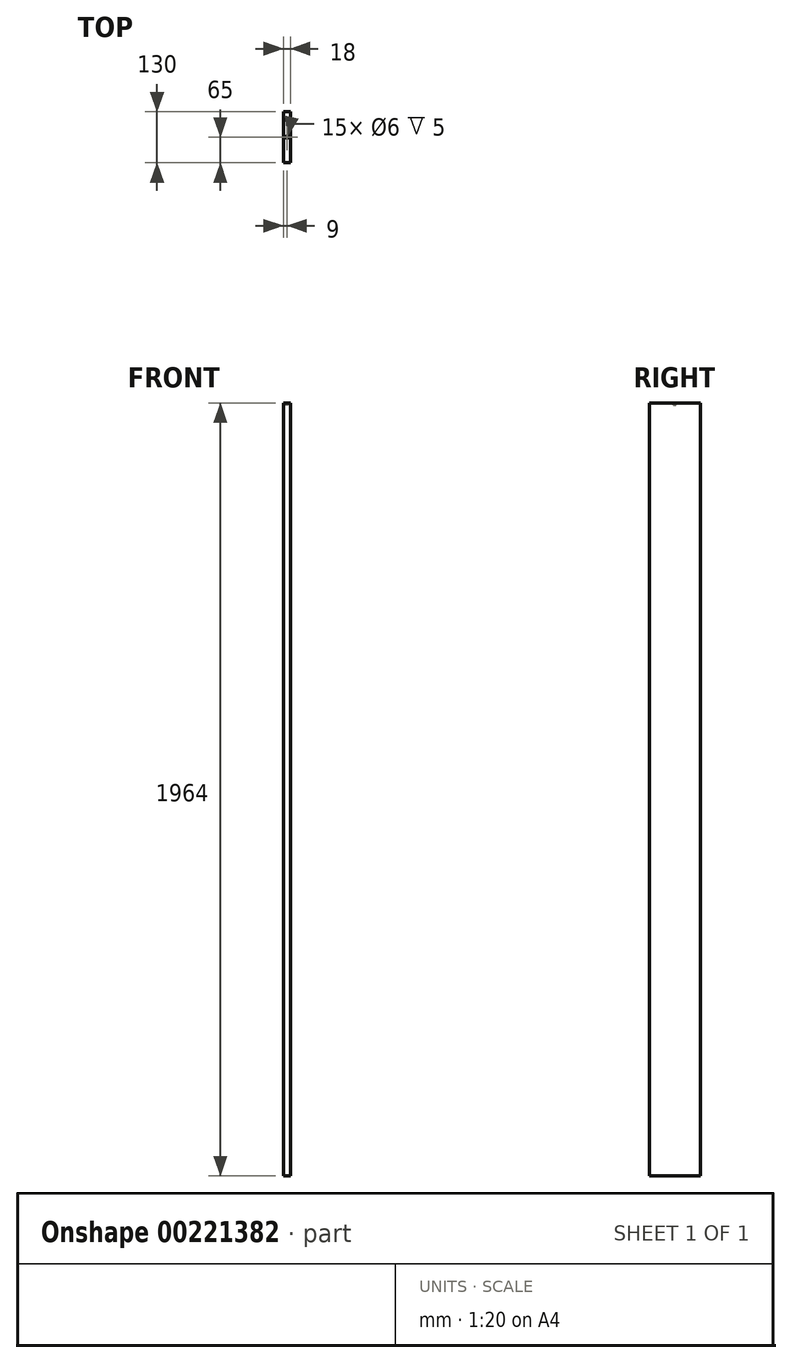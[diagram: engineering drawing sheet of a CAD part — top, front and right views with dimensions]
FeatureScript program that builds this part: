
annotation { "Feature Type Name" : "Feature", "Feature Type Description" : "" }
export const myFeature = defineFeature(function(context is Context, id is Id, definition is map)
    precondition{}
    {
        {
            var Q0;
            Q0=qCreatedBy(makeId("Right.planeOp"),FACE);
            var sketch = newSketch(context, id + "F0", { "sketchPlane" : qUnion([Q0])});
            skLineSegment(sketch, "E0.bottom", {"start": v(65, -982) * mm, "end": v(-65, -982) * mm});
            skLineSegment(sketch, "E0.top", {"start": v(65, 982) * mm, "end": v(-65, 982) * mm});
            skLineSegment(sketch, "E0.left", {"start": v(65, -982) * mm, "end": v(65, 982) * mm});
            skLineSegment(sketch, "E0.right", {"start": v(-65, -982) * mm, "end": v(-65, 982) * mm});
            skPoint(sketch, "E0.middle", {"position": v(0, 0) * mm});
            skSolve(sketch);
        }
        {
            var Q0;
            Q0=qSketchRegion(id+"F0",true);
            extrude(context, id + "F1", {"entities" : qUnion([Q0]), "depth" : 18 * mm});
        }
        {
            var Q0;
            Q0=makeQuery(id+"F1.opExtrude","SWEPT_FACE",FACE,{"disambiguationData":[OSD([sQuery(id+"F0.wireOp",EDGE,"E0.top")])]});
            var sketch = newSketch(context, id + "F2", { "sketchPlane" : qUnion([Q0])});
            skCircle(sketch, "E1", {"center": v(9, 0) * mm, "radius": 3 * mm});
            skSolve(sketch);
        }
        {
            var Q0;
            Q0=qSketchRegion(id+"F2",true);
            extrude(context, id + "F3", {"entities" : qUnion([Q0]), "operationType" : NewBodyOperationType.REMOVE, "oppositeDirection" : true, "depth" : 5 * mm});
        }
    });
